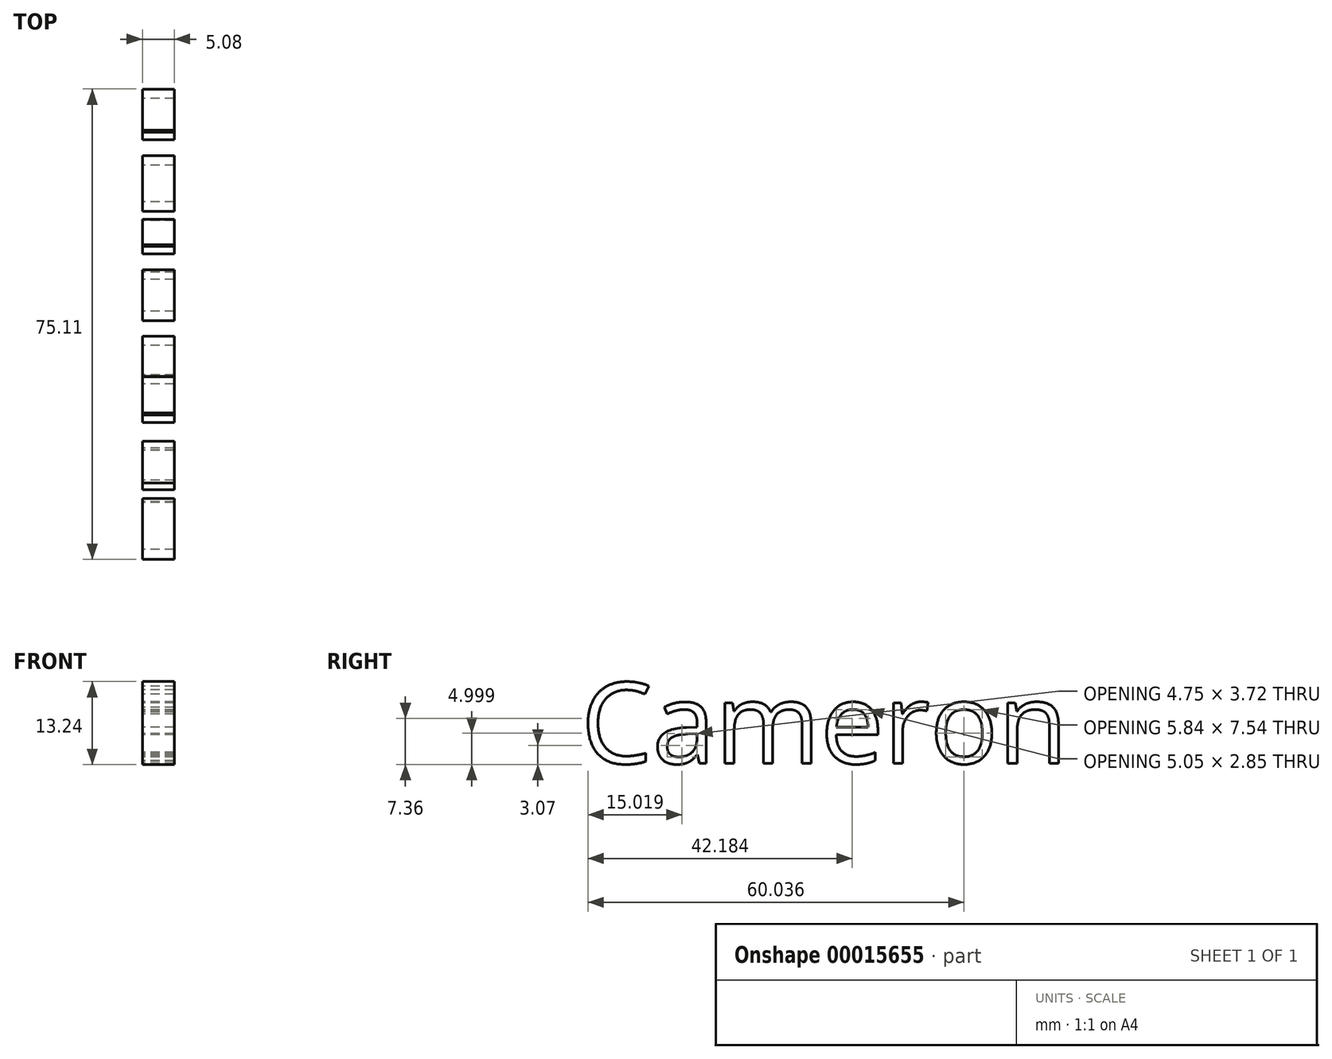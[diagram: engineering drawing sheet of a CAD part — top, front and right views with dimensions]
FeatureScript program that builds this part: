
annotation { "Feature Type Name" : "Feature", "Feature Type Description" : "" }
export const myFeature = defineFeature(function(context is Context, id is Id, definition is map)
    precondition{}
    {
        {
            var Q0;
            Q0=qCreatedBy(makeId("Top.planeOp"),FACE);
            var sketch = newSketch(context, id + "F0", { "sketchPlane" : qUnion([Q0])});
            skText(sketch, "E0", { "text": "Cameron\n", "fontName": "OpenSans-Regular.ttf"});
            const initialGuessF0  = {"E0": [-0.01246, -0.00578, 1, 0, 0.01299]};
            skSetInitialGuess(sketch, initialGuessF0);
            skSolve(sketch);
        }
        {
            var Q0;
            Q0 = qSketchRegion(id + "F0", true);
            extrude(context, id + "F1", {"entities" : qUnion([Q0]), "depth" : 5.08 * mm});
        }
        {
            var Q0;
            Q0=makeQuery(id+"F1.opExtrude","SWEPT_BODY",BODY,{"disambiguationData":[OSD([sQuery(id+"F0.wireOp",EDGE,"E0.sketch_text.stroke-0"),sQuery(id+"F0.wireOp",EDGE,"E0.sketch_text.stroke-1"),sQuery(id+"F0.wireOp",EDGE,"E0.sketch_text.stroke-2"),sQuery(id+"F0.wireOp",EDGE,"E0.sketch_text.stroke-3"),sQuery(id+"F0.wireOp",EDGE,"E0.sketch_text.stroke-4"),sQuery(id+"F0.wireOp",EDGE,"E0.sketch_text.stroke-5"),sQuery(id+"F0.wireOp",EDGE,"E0.sketch_text.stroke-6"),sQuery(id+"F0.wireOp",EDGE,"E0.sketch_text.stroke-7"),sQuery(id+"F0.wireOp",EDGE,"E0.sketch_text.stroke-8"),sQuery(id+"F0.wireOp",EDGE,"E0.sketch_text.stroke-9"),sQuery(id+"F0.wireOp",EDGE,"E0.sketch_text.stroke-10"),sQuery(id+"F0.wireOp",EDGE,"E0.sketch_text.stroke-11"),sQuery(id+"F0.wireOp",EDGE,"E0.sketch_text.stroke-12"),sQuery(id+"F0.wireOp",EDGE,"E0.sketch_text.stroke-13"),sQuery(id+"F0.wireOp",EDGE,"E0.sketch_text.stroke-14")])]});
            deleteBodies(context, id + "F2", {"entities" : qUnion([Q0])});
        }
        {
            var Q0;
            Q0=makeQuery(id+"F1.opExtrude","SWEPT_BODY",BODY,{"disambiguationData":[OSD([sQuery(id+"F0.wireOp",EDGE,"E0.sketch_text.stroke-15"),sQuery(id+"F0.wireOp",EDGE,"E0.sketch_text.stroke-16"),sQuery(id+"F0.wireOp",EDGE,"E0.sketch_text.stroke-17"),sQuery(id+"F0.wireOp",EDGE,"E0.sketch_text.stroke-18"),sQuery(id+"F0.wireOp",EDGE,"E0.sketch_text.stroke-19"),sQuery(id+"F0.wireOp",EDGE,"E0.sketch_text.stroke-20"),sQuery(id+"F0.wireOp",EDGE,"E0.sketch_text.stroke-21"),sQuery(id+"F0.wireOp",EDGE,"E0.sketch_text.stroke-22"),sQuery(id+"F0.wireOp",EDGE,"E0.sketch_text.stroke-23"),sQuery(id+"F0.wireOp",EDGE,"E0.sketch_text.stroke-24"),sQuery(id+"F0.wireOp",EDGE,"E0.sketch_text.stroke-25"),sQuery(id+"F0.wireOp",EDGE,"E0.sketch_text.stroke-26"),sQuery(id+"F0.wireOp",EDGE,"E0.sketch_text.stroke-27"),sQuery(id+"F0.wireOp",EDGE,"E0.sketch_text.stroke-28"),sQuery(id+"F0.wireOp",EDGE,"E0.sketch_text.stroke-29"),sQuery(id+"F0.wireOp",EDGE,"E0.sketch_text.stroke-30"),sQuery(id+"F0.wireOp",EDGE,"E0.sketch_text.stroke-31"),sQuery(id+"F0.wireOp",EDGE,"E0.sketch_text.stroke-32"),sQuery(id+"F0.wireOp",EDGE,"E0.sketch_text.stroke-33"),sQuery(id+"F0.wireOp",EDGE,"E0.sketch_text.stroke-34"),sQuery(id+"F0.wireOp",EDGE,"E0.sketch_text.stroke-35"),sQuery(id+"F0.wireOp",EDGE,"E0.sketch_text.stroke-36"),sQuery(id+"F0.wireOp",EDGE,"E0.sketch_text.stroke-37"),sQuery(id+"F0.wireOp",EDGE,"E0.sketch_text.stroke-38"),sQuery(id+"F0.wireOp",EDGE,"E0.sketch_text.stroke-39"),sQuery(id+"F0.wireOp",EDGE,"E0.sketch_text.stroke-40"),sQuery(id+"F0.wireOp",EDGE,"E0.sketch_text.stroke-41")])]});
            deleteBodies(context, id + "F3", {"entities" : qUnion([Q0])});
        }
        {
            var Q0;
            Q0=makeQuery(id+"F1.opExtrude","SWEPT_BODY",BODY,{"disambiguationData":[OSD([sQuery(id+"F0.wireOp",EDGE,"E0.sketch_text.stroke-42"),sQuery(id+"F0.wireOp",EDGE,"E0.sketch_text.stroke-43"),sQuery(id+"F0.wireOp",EDGE,"E0.sketch_text.stroke-44"),sQuery(id+"F0.wireOp",EDGE,"E0.sketch_text.stroke-45"),sQuery(id+"F0.wireOp",EDGE,"E0.sketch_text.stroke-46"),sQuery(id+"F0.wireOp",EDGE,"E0.sketch_text.stroke-47"),sQuery(id+"F0.wireOp",EDGE,"E0.sketch_text.stroke-48"),sQuery(id+"F0.wireOp",EDGE,"E0.sketch_text.stroke-49"),sQuery(id+"F0.wireOp",EDGE,"E0.sketch_text.stroke-50"),sQuery(id+"F0.wireOp",EDGE,"E0.sketch_text.stroke-51"),sQuery(id+"F0.wireOp",EDGE,"E0.sketch_text.stroke-52"),sQuery(id+"F0.wireOp",EDGE,"E0.sketch_text.stroke-53"),sQuery(id+"F0.wireOp",EDGE,"E0.sketch_text.stroke-54"),sQuery(id+"F0.wireOp",EDGE,"E0.sketch_text.stroke-55"),sQuery(id+"F0.wireOp",EDGE,"E0.sketch_text.stroke-56"),sQuery(id+"F0.wireOp",EDGE,"E0.sketch_text.stroke-57"),sQuery(id+"F0.wireOp",EDGE,"E0.sketch_text.stroke-58"),sQuery(id+"F0.wireOp",EDGE,"E0.sketch_text.stroke-59"),sQuery(id+"F0.wireOp",EDGE,"E0.sketch_text.stroke-60"),sQuery(id+"F0.wireOp",EDGE,"E0.sketch_text.stroke-61"),sQuery(id+"F0.wireOp",EDGE,"E0.sketch_text.stroke-62"),sQuery(id+"F0.wireOp",EDGE,"E0.sketch_text.stroke-63"),sQuery(id+"F0.wireOp",EDGE,"E0.sketch_text.stroke-64"),sQuery(id+"F0.wireOp",EDGE,"E0.sketch_text.stroke-65"),sQuery(id+"F0.wireOp",EDGE,"E0.sketch_text.stroke-66"),sQuery(id+"F0.wireOp",EDGE,"E0.sketch_text.stroke-67"),sQuery(id+"F0.wireOp",EDGE,"E0.sketch_text.stroke-68"),sQuery(id+"F0.wireOp",EDGE,"E0.sketch_text.stroke-69")])]});
            deleteBodies(context, id + "F4", {"entities" : qUnion([Q0])});
        }
        {
            var Q0;
            Q0=makeQuery(id+"F1.opExtrude","SWEPT_BODY",BODY,{"disambiguationData":[OSD([sQuery(id+"F0.wireOp",EDGE,"E0.sketch_text.stroke-70"),sQuery(id+"F0.wireOp",EDGE,"E0.sketch_text.stroke-71"),sQuery(id+"F0.wireOp",EDGE,"E0.sketch_text.stroke-72"),sQuery(id+"F0.wireOp",EDGE,"E0.sketch_text.stroke-73"),sQuery(id+"F0.wireOp",EDGE,"E0.sketch_text.stroke-74"),sQuery(id+"F0.wireOp",EDGE,"E0.sketch_text.stroke-75"),sQuery(id+"F0.wireOp",EDGE,"E0.sketch_text.stroke-76"),sQuery(id+"F0.wireOp",EDGE,"E0.sketch_text.stroke-77"),sQuery(id+"F0.wireOp",EDGE,"E0.sketch_text.stroke-78"),sQuery(id+"F0.wireOp",EDGE,"E0.sketch_text.stroke-79"),sQuery(id+"F0.wireOp",EDGE,"E0.sketch_text.stroke-80"),sQuery(id+"F0.wireOp",EDGE,"E0.sketch_text.stroke-81"),sQuery(id+"F0.wireOp",EDGE,"E0.sketch_text.stroke-82"),sQuery(id+"F0.wireOp",EDGE,"E0.sketch_text.stroke-83"),sQuery(id+"F0.wireOp",EDGE,"E0.sketch_text.stroke-84"),sQuery(id+"F0.wireOp",EDGE,"E0.sketch_text.stroke-85"),sQuery(id+"F0.wireOp",EDGE,"E0.sketch_text.stroke-86"),sQuery(id+"F0.wireOp",EDGE,"E0.sketch_text.stroke-87"),sQuery(id+"F0.wireOp",EDGE,"E0.sketch_text.stroke-88")])]});
            deleteBodies(context, id + "F5", {"entities" : qUnion([Q0])});
        }
        {
            var Q0;
            Q0=makeQuery(id+"F1.opExtrude","SWEPT_BODY",BODY,{"disambiguationData":[OSD([sQuery(id+"F0.wireOp",EDGE,"E0.sketch_text.stroke-89"),sQuery(id+"F0.wireOp",EDGE,"E0.sketch_text.stroke-90"),sQuery(id+"F0.wireOp",EDGE,"E0.sketch_text.stroke-91"),sQuery(id+"F0.wireOp",EDGE,"E0.sketch_text.stroke-92"),sQuery(id+"F0.wireOp",EDGE,"E0.sketch_text.stroke-93"),sQuery(id+"F0.wireOp",EDGE,"E0.sketch_text.stroke-94"),sQuery(id+"F0.wireOp",EDGE,"E0.sketch_text.stroke-95"),sQuery(id+"F0.wireOp",EDGE,"E0.sketch_text.stroke-96"),sQuery(id+"F0.wireOp",EDGE,"E0.sketch_text.stroke-97"),sQuery(id+"F0.wireOp",EDGE,"E0.sketch_text.stroke-98"),sQuery(id+"F0.wireOp",EDGE,"E0.sketch_text.stroke-99"),sQuery(id+"F0.wireOp",EDGE,"E0.sketch_text.stroke-100"),sQuery(id+"F0.wireOp",EDGE,"E0.sketch_text.stroke-101")])]});
            deleteBodies(context, id + "F6", {"entities" : qUnion([Q0])});
        }
        {
            var Q0;
            Q0=makeQuery(id+"F1.opExtrude","SWEPT_BODY",BODY,{"disambiguationData":[OSD([sQuery(id+"F0.wireOp",EDGE,"E0.sketch_text.stroke-102"),sQuery(id+"F0.wireOp",EDGE,"E0.sketch_text.stroke-103"),sQuery(id+"F0.wireOp",EDGE,"E0.sketch_text.stroke-104"),sQuery(id+"F0.wireOp",EDGE,"E0.sketch_text.stroke-105"),sQuery(id+"F0.wireOp",EDGE,"E0.sketch_text.stroke-106"),sQuery(id+"F0.wireOp",EDGE,"E0.sketch_text.stroke-107"),sQuery(id+"F0.wireOp",EDGE,"E0.sketch_text.stroke-108"),sQuery(id+"F0.wireOp",EDGE,"E0.sketch_text.stroke-109"),sQuery(id+"F0.wireOp",EDGE,"E0.sketch_text.stroke-110"),sQuery(id+"F0.wireOp",EDGE,"E0.sketch_text.stroke-111"),sQuery(id+"F0.wireOp",EDGE,"E0.sketch_text.stroke-112"),sQuery(id+"F0.wireOp",EDGE,"E0.sketch_text.stroke-113"),sQuery(id+"F0.wireOp",EDGE,"E0.sketch_text.stroke-114"),sQuery(id+"F0.wireOp",EDGE,"E0.sketch_text.stroke-115"),sQuery(id+"F0.wireOp",EDGE,"E0.sketch_text.stroke-116"),sQuery(id+"F0.wireOp",EDGE,"E0.sketch_text.stroke-117"),sQuery(id+"F0.wireOp",EDGE,"E0.sketch_text.stroke-118")])]});
            deleteBodies(context, id + "F7", {"entities" : qUnion([Q0])});
        }
        {
            var Q0;
            Q0=makeQuery(id+"F1.opExtrude","SWEPT_BODY",BODY,{"disambiguationData":[OSD([sQuery(id+"F0.wireOp",EDGE,"E0.sketch_text.stroke-119"),sQuery(id+"F0.wireOp",EDGE,"E0.sketch_text.stroke-120"),sQuery(id+"F0.wireOp",EDGE,"E0.sketch_text.stroke-121"),sQuery(id+"F0.wireOp",EDGE,"E0.sketch_text.stroke-122"),sQuery(id+"F0.wireOp",EDGE,"E0.sketch_text.stroke-123"),sQuery(id+"F0.wireOp",EDGE,"E0.sketch_text.stroke-124"),sQuery(id+"F0.wireOp",EDGE,"E0.sketch_text.stroke-125"),sQuery(id+"F0.wireOp",EDGE,"E0.sketch_text.stroke-126"),sQuery(id+"F0.wireOp",EDGE,"E0.sketch_text.stroke-127"),sQuery(id+"F0.wireOp",EDGE,"E0.sketch_text.stroke-128"),sQuery(id+"F0.wireOp",EDGE,"E0.sketch_text.stroke-129"),sQuery(id+"F0.wireOp",EDGE,"E0.sketch_text.stroke-130"),sQuery(id+"F0.wireOp",EDGE,"E0.sketch_text.stroke-131"),sQuery(id+"F0.wireOp",EDGE,"E0.sketch_text.stroke-132"),sQuery(id+"F0.wireOp",EDGE,"E0.sketch_text.stroke-133"),sQuery(id+"F0.wireOp",EDGE,"E0.sketch_text.stroke-134"),sQuery(id+"F0.wireOp",EDGE,"E0.sketch_text.stroke-135")])]});
            deleteBodies(context, id + "F8", {"entities" : qUnion([Q0])});
        }
        {
            var Q0;
            Q0=qCreatedBy(makeId("Right.planeOp"),FACE);
            var sketch = newSketch(context, id + "F9", { "sketchPlane" : qUnion([Q0])});
            skText(sketch, "E1", { "text": "Cameron\n", "fontName": "OpenSans-Regular.ttf"});
            const initialGuessF9  = {"E1": [-0.02908, 0.00302, 1, 0, 0.01299]};
            skSetInitialGuess(sketch, initialGuessF9);
            skSolve(sketch);
        }
        {
            var Q0;
            Q0 = qSketchRegion(id + "F9", true);
            extrude(context, id + "F10", {"entities" : qUnion([Q0]), "depth" : 5.08 * mm});
        }
    });
